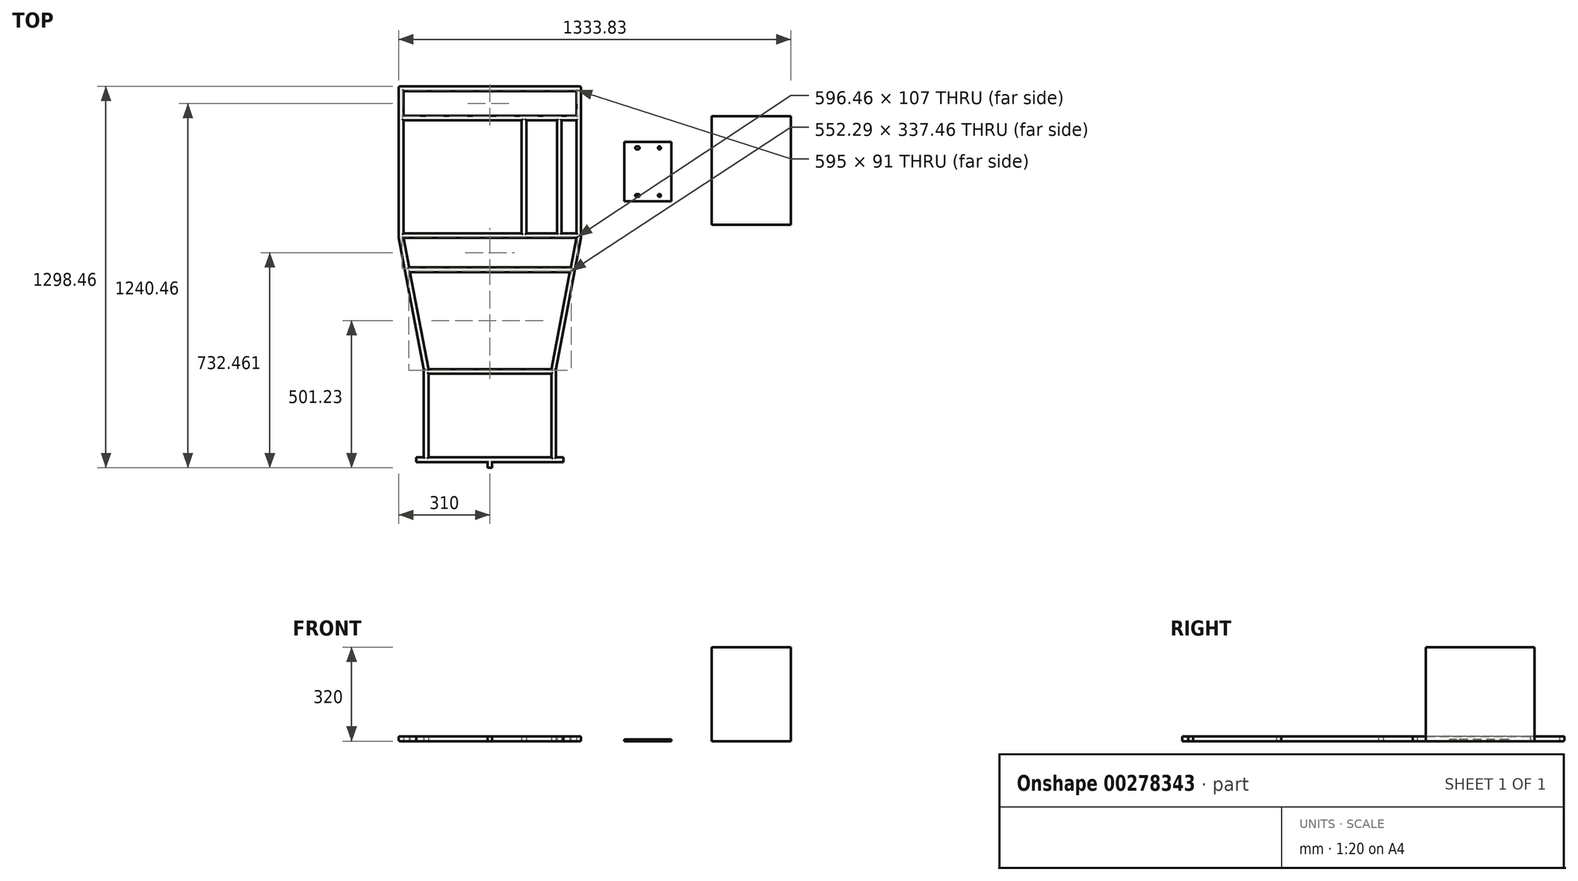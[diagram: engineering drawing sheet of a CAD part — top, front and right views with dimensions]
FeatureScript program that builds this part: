
annotation { "Feature Type Name" : "Feature", "Feature Type Description" : "" }
export const myFeature = defineFeature(function(context is Context, id is Id, definition is map)
    precondition{}
    {
        {
            var Q0;
            Q0=qCreatedBy(makeId("Top.planeOp"),FACE);
            var sketch = newSketch(context, id + "F0", { "sketchPlane" : qUnion([Q0])});
            skLineSegment(sketch, "E0", {"start": v(0, 0) * mm, "end": v(0, 589.23) * mm, "construction": true});
            skLineSegment(sketch, "E1", {"start": v(0, 0) * mm, "end": v(0, -589.23) * mm, "construction": true});
            skLineSegment(sketch, "E2", {"start": v(0, -589.23) * mm, "end": v(-225, -589.23) * mm, "construction": true});
            skLineSegment(sketch, "E3", {"start": v(0, -589.23) * mm, "end": v(225, -589.23) * mm, "construction": true});
            skLineSegment(sketch, "E4", {"start": v(0, 589.23) * mm, "end": v(-310, 589.23) * mm, "construction": true});
            skLineSegment(sketch, "E5", {"start": v(0, 589.23) * mm, "end": v(310, 589.23) * mm, "construction": true});
            skLineSegment(sketch, "E6", {"start": v(225, -589.23) * mm, "end": v(-225, -589.23) * mm});
            skLineSegment(sketch, "E7", {"start": v(310, 589.23) * mm, "end": v(-310, 589.23) * mm});
            skLineSegment(sketch, "E8.0", {"start": v(294, 573.23) * mm, "end": v(-294, 573.23) * mm});
            skLineSegment(sketch, "E8.2", {"start": v(209, -573.23) * mm, "end": v(-209, -573.23) * mm});
            skLineSegment(sketch, "E9", {"start": v(-225, -589.23) * mm, "end": v(-225, -684.23) * mm});
            skLineSegment(sketch, "E10", {"start": v(225, -589.23) * mm, "end": v(225, -684.23) * mm});
            skLineSegment(sketch, "E11", {"start": v(220, -689.23) * mm, "end": v(-220, -689.23) * mm});
            skLineSegment(sketch, "E12.0", {"start": v(209, -589.23) * mm, "end": v(209, -673.23) * mm});
            skLineSegment(sketch, "E12.1", {"start": v(209, -673.23) * mm, "end": v(-209, -673.23) * mm});
            skLineSegment(sketch, "E12.2", {"start": v(-209, -589.23) * mm, "end": v(-209, -673.23) * mm});
            skPoint(sketch, "E13.visualSharp", {"position": v(-225, -689.23) * mm});
            skArc(sketch, "E13.filletArc", {"start": v(-225, -684.23) * mm, "mid": v(-223.54, -687.77) * mm, "end": v(-220, -689.23) * mm});
            skPoint(sketch, "E14.visualSharp", {"position": v(225, -689.23) * mm});
            skArc(sketch, "E14.filletArc", {"start": v(220, -689.23) * mm, "mid": v(223.54, -687.77) * mm, "end": v(225, -684.23) * mm});
            skLineSegment(sketch, "E15", {"start": v(-310, 589.23) * mm, "end": v(-310, 684.23) * mm});
            skLineSegment(sketch, "E16", {"start": v(-305, 689.23) * mm, "end": v(305, 689.23) * mm});
            skLineSegment(sketch, "E17", {"start": v(310, 684.23) * mm, "end": v(310, 589.23) * mm});
            skLineSegment(sketch, "E18.0", {"start": v(294, 673.23) * mm, "end": v(294, 589.23) * mm});
            skLineSegment(sketch, "E18.1", {"start": v(-294, 673.23) * mm, "end": v(294, 673.23) * mm});
            skLineSegment(sketch, "E18.2", {"start": v(-294, 589.23) * mm, "end": v(-294, 673.23) * mm});
            skPoint(sketch, "E19.visualSharp", {"position": v(-310, 689.23) * mm});
            skArc(sketch, "E19.filletArc", {"start": v(-305, 689.23) * mm, "mid": v(-308.54, 687.77) * mm, "end": v(-310, 684.23) * mm});
            skPoint(sketch, "E20.visualSharp", {"position": v(310, 689.23) * mm});
            skArc(sketch, "E20.filletArc", {"start": v(310, 684.23) * mm, "mid": v(308.54, 687.77) * mm, "end": v(305, 689.23) * mm});
            skLineSegment(sketch, "E21", {"start": v(-294, 573.23) * mm, "end": v(-294, 173.23) * mm});
            skLineSegment(sketch, "E22", {"start": v(294, 573.23) * mm, "end": v(294, 173.23) * mm});
            skLineSegment(sketch, "E23", {"start": v(-310, 589.23) * mm, "end": v(-310, 173.23) * mm});
            skLineSegment(sketch, "E24", {"start": v(310, 589.23) * mm, "end": v(310, 173.23) * mm});
            skLineSegment(sketch, "E25", {"start": v(-209, -573.23) * mm, "end": v(-209, -273.23) * mm});
            skLineSegment(sketch, "E26", {"start": v(209, -573.23) * mm, "end": v(209, -273.23) * mm});
            skLineSegment(sketch, "E27", {"start": v(225, -589.23) * mm, "end": v(225, -273.23) * mm});
            skLineSegment(sketch, "E28", {"start": v(-225, -589.23) * mm, "end": v(-225, -273.23) * mm});
            skLineSegment(sketch, "E29", {"start": v(310, 173.23) * mm, "end": v(225, -273.23) * mm});
            skLineSegment(sketch, "E30", {"start": v(209, -273.23) * mm, "end": v(294, 173.23) * mm});
            skLineSegment(sketch, "E31", {"start": v(-209, -273.23) * mm, "end": v(-294, 173.23) * mm});
            skLineSegment(sketch, "E32", {"start": v(-225, -273.23) * mm, "end": v(-310, 173.23) * mm});
            skLineSegment(sketch, "E33", {"start": v(-294, 203.23) * mm, "end": v(294, 203.23) * mm, "construction": true});
            skLineSegment(sketch, "E34", {"start": v(-209, -273.23) * mm, "end": v(209, -273.23) * mm});
            skLineSegment(sketch, "E35", {"start": v(-209, -289.23) * mm, "end": v(209, -289.23) * mm});
            skLineSegment(sketch, "E36", {"start": v(294, 173.23) * mm, "end": v(-294, 173.23) * mm});
            skLineSegment(sketch, "E37", {"start": v(-294, 189.23) * mm, "end": v(294, 189.23) * mm});
            skLineSegment(sketch, "E38", {"start": v(244, 573.23) * mm, "end": v(244, 189.23) * mm});
            skLineSegment(sketch, "E39", {"start": v(228, 573.23) * mm, "end": v(228, 189.23) * mm});
            skLineSegment(sketch, "E40", {"start": v(124, 573.23) * mm, "end": v(124, 189.23) * mm});
            skLineSegment(sketch, "E41", {"start": v(108, 573.23) * mm, "end": v(108, 189.23) * mm});
            skLineSegment(sketch, "E42", {"start": v(116, 573.23) * mm, "end": v(116, 189.23) * mm, "construction": true});
            skLineSegment(sketch, "E43", {"start": v(236, 189.23) * mm, "end": v(236, 573.23) * mm, "construction": true});
            skLineSegment(sketch, "E44", {"start": v(-271.92, 57.23) * mm, "end": v(271.92, 57.23) * mm});
            skLineSegment(sketch, "E45", {"start": v(271.92, 57.23) * mm, "end": v(274.96, 73.23) * mm});
            skLineSegment(sketch, "E46", {"start": v(274.96, 73.23) * mm, "end": v(-274.96, 73.23) * mm});
            skLineSegment(sketch, "E47", {"start": v(225, -589.23) * mm, "end": v(250, -589.23) * mm});
            skLineSegment(sketch, "E48", {"start": v(250, -589.23) * mm, "end": v(250, -573.23) * mm});
            skLineSegment(sketch, "E49", {"start": v(250, -573.23) * mm, "end": v(225, -573.23) * mm});
            skLineSegment(sketch, "E50", {"start": v(-225, -589.23) * mm, "end": v(-250, -589.23) * mm});
            skLineSegment(sketch, "E51", {"start": v(-250, -589.23) * mm, "end": v(-250, -573.23) * mm});
            skLineSegment(sketch, "E52", {"start": v(-250, -573.23) * mm, "end": v(-225, -573.23) * mm});
            skLineSegment(sketch, "E53", {"start": v(-8, -589.23) * mm, "end": v(-8, -609.23) * mm});
            skLineSegment(sketch, "E54", {"start": v(-8, -609.23) * mm, "end": v(8, -609.23) * mm});
            skLineSegment(sketch, "E55", {"start": v(8, -609.23) * mm, "end": v(8, -589.23) * mm});
            skLineSegment(sketch, "E56", {"start": v(0, -589.23) * mm, "end": v(0, -609.23) * mm, "construction": true});
            skSolve(sketch);
        }
        {
            var Q0;
            {var subQ0=sQuery(id+"F0.wireOp",EDGE,"E15");Q0=makeQuery(id+"F0.imprint","IMPRINT",FACE,{"disambiguationData":[TD([[makeQuery(id+"F0.imprint","IMPRINT",EDGE,{"derivedFrom":subQ0}),-1.0]])]});}
            var Q1;
            {var subQ8=sQuery(id+"F0.wireOp",EDGE,"E8.0");Q1=makeQuery(id+"F0.imprint","IMPRINT",FACE,{"disambiguationData":[TD([[makeQuery(id+"F0.imprint","IMPRINT",EDGE,{"derivedFrom":subQ8}),-1.0]])]});}
            var Q2;
            {var subQ0=sQuery(id+"F0.wireOp",EDGE,"E33");Q2=makeQuery(id+"F0.imprint","IMPRINT",FACE,{"disambiguationData":[TD([[makeQuery(id+"F0.imprint","IMPRINT",EDGE,{"derivedFrom":subQ0}),1.0]])]});}
            var Q3;
            {var subQ0=sQuery(id+"F0.wireOp",EDGE,"E34");Q3=makeQuery(id+"F0.imprint","IMPRINT",FACE,{"disambiguationData":[TD([[makeQuery(id+"F0.imprint","IMPRINT",EDGE,{"derivedFrom":subQ0}),-1.0]])]});}
            var Q4;
            {var subQ0=sQuery(id+"F0.wireOp",EDGE,"E36");Q4=makeQuery(id+"F0.imprint","IMPRINT",FACE,{"disambiguationData":[TD([[makeQuery(id+"F0.imprint","IMPRINT",EDGE,{"derivedFrom":subQ0}),-1.0]])]});}
            var Q5;
            {var subQ0=sQuery(id+"F0.wireOp",EDGE,"E40");Q5=makeQuery(id+"F0.imprint","IMPRINT",FACE,{"disambiguationData":[TD([[makeQuery(id+"F0.imprint","IMPRINT",EDGE,{"derivedFrom":subQ0}),-1.0]])]});}
            var Q6;
            {var subQ0=sQuery(id+"F0.wireOp",EDGE,"E38");Q6=makeQuery(id+"F0.imprint","IMPRINT",FACE,{"disambiguationData":[TD([[makeQuery(id+"F0.imprint","IMPRINT",EDGE,{"derivedFrom":subQ0}),-1.0]])]});}
            var Q7;
            {var subQ0=sQuery(id+"F0.wireOp",EDGE,"E44");Q7=makeQuery(id+"F0.imprint","IMPRINT",FACE,{"disambiguationData":[TD([[makeQuery(id+"F0.imprint","IMPRINT",EDGE,{"derivedFrom":subQ0}),1.0]])]});}
            var Q8;
            {var subQ0=sQuery(id+"F0.wireOp",EDGE,"E50");Q8=makeQuery(id+"F0.imprint","IMPRINT",FACE,{"disambiguationData":[TD([[makeQuery(id+"F0.imprint","IMPRINT",EDGE,{"derivedFrom":subQ0}),-1.0]])]});}
            var Q9;
            {var subQ0=sQuery(id+"F0.wireOp",EDGE,"E47");Q9=makeQuery(id+"F0.imprint","IMPRINT",FACE,{"disambiguationData":[TD([[makeQuery(id+"F0.imprint","IMPRINT",EDGE,{"derivedFrom":subQ0}),1.0]])]});}
            var Q10;
            {var subQ0=sQuery(id+"F0.wireOp",EDGE,"E53");Q10=makeQuery(id+"F0.imprint","IMPRINT",FACE,{"disambiguationData":[TD([[makeQuery(id+"F0.imprint","IMPRINT",EDGE,{"derivedFrom":subQ0}),1.0]])]});}
            extrude(context, id + "F1", {"entities" : qUnion([Q0, Q1, Q2, Q3, Q4, Q5, Q6, Q7, Q8, Q9, Q10]), "depth" : 16 * mm});
        }
        {
            var Q0;
            Q0=makeQuery(id+"F1.opExtrude","CAP_EDGE",EDGE,{"disambiguationData":[OSD([sQuery(id+"F0.wireOp",EDGE,"E10")])],"isStart":false});
            var Q1;
            Q1=makeQuery(id+"F1.opExtrude","CAP_EDGE",EDGE,{"disambiguationData":[OSD([sQuery(id+"F0.wireOp",EDGE,"xuW9dsa4-weEu-yKkH-qgbv-HWIhfIHViFJe")])],"isStart":false});
            var Q2;
            Q2=makeQuery(id+"F1.opExtrude","CAP_EDGE",EDGE,{"disambiguationData":[OSD([sQuery(id+"F0.wireOp",EDGE,"E6")])],"isStart":false});
            var Q3;
            Q3=makeQuery(id+"F1.opExtrude","CAP_EDGE",EDGE,{"disambiguationData":[OSD([sQuery(id+"F0.wireOp",EDGE,"E8.2")])],"isStart":false});
            var Q4;
            Q4=makeQuery(id+"F1.opExtrude","CAP_EDGE",EDGE,{"disambiguationData":[OSD([sQuery(id+"F0.wireOp",EDGE,"E8.3")])],"isStart":false});
            var Q5;
            Q5=makeQuery(id+"F1.opExtrude","CAP_EDGE",EDGE,{"disambiguationData":[OSD([sQuery(id+"F0.wireOp",EDGE,"E12.2")])],"isStart":false});
            var Q6;
            Q6=makeQuery(id+"F1.opExtrude","CAP_EDGE",EDGE,{"disambiguationData":[OSD([sQuery(id+"F0.wireOp",EDGE,"E8.0")])],"isStart":false});
            var Q7;
            Q7=makeQuery(id+"F1.opExtrude","CAP_EDGE",EDGE,{"disambiguationData":[OSD([sQuery(id+"F0.wireOp",EDGE,"E7")])],"isStart":false});
            var Q8;
            Q8=makeQuery(id+"F1.opExtrude","CAP_EDGE",EDGE,{"disambiguationData":[OSD([sQuery(id+"F0.wireOp",EDGE,"E18.1")])],"isStart":false});
            var Q9;
            Q9=makeQuery(id+"F1.opExtrude","CAP_EDGE",EDGE,{"disambiguationData":[OSD([sQuery(id+"F0.wireOp",EDGE,"E16")])],"isStart":false});
            var Q10;
            Q10=makeQuery(id+"F1.opExtrude","CAP_EDGE",EDGE,{"disambiguationData":[OSD([sQuery(id+"F0.wireOp",EDGE,"E17")])],"isStart":false});
            var Q11;
            Q11=makeQuery(id+"F1.opExtrude","CAP_EDGE",EDGE,{"disambiguationData":[OSD([sQuery(id+"F0.wireOp",EDGE,"E18.0")])],"isStart":false});
            var Q12;
            Q12=makeQuery(id+"F1.opExtrude","CAP_EDGE",EDGE,{"disambiguationData":[OSD([sQuery(id+"F0.wireOp",EDGE,"E18.2")])],"isStart":false});
            var Q13;
            Q13=makeQuery(id+"F1.opExtrude","CAP_EDGE",EDGE,{"disambiguationData":[OSD([sQuery(id+"F0.wireOp",EDGE,"kNVx2aqo-1R29-r8ME-eJTo-0D4SkdkJlZAj")])],"isStart":false});
            var Q14;
            Q14=makeQuery(id+"F1.opExtrude","CAP_EDGE",EDGE,{"disambiguationData":[OSD([sQuery(id+"F0.wireOp",EDGE,"kNVx2aqo-1R29-r8ME-eJTo-0D4SkdkJlZAj")])],"isStart":true});
            var Q15;
            Q15=makeQuery(id+"F1.opExtrude","CAP_EDGE",EDGE,{"disambiguationData":[OSD([sQuery(id+"F0.wireOp",EDGE,"E15")])],"isStart":false});
            var Q16;
            Q16=makeQuery(id+"F1.opExtrude","CAP_EDGE",EDGE,{"disambiguationData":[OSD([sQuery(id+"F0.wireOp",EDGE,"E16")])],"isStart":true});
            var Q17;
            Q17=makeQuery(id+"F1.opExtrude","CAP_EDGE",EDGE,{"disambiguationData":[OSD([sQuery(id+"F0.wireOp",EDGE,"E8.1")])],"isStart":true});
            var Q18;
            Q18=makeQuery(id+"F1.opExtrude","CAP_EDGE",EDGE,{"disambiguationData":[OSD([sQuery(id+"F0.wireOp",EDGE,"E8.2")])],"isStart":true});
            var Q19;
            Q19=makeQuery(id+"F1.opExtrude","CAP_EDGE",EDGE,{"disambiguationData":[OSD([sQuery(id+"F0.wireOp",EDGE,"E12.1")])],"isStart":true});
            var Q20;
            Q20=makeQuery(id+"F1.opExtrude","CAP_EDGE",EDGE,{"disambiguationData":[OSD([sQuery(id+"F0.wireOp",EDGE,"E12.2")])],"isStart":true});
            var Q21;
            Q21=makeQuery(id+"F1.opExtrude","CAP_EDGE",EDGE,{"disambiguationData":[OSD([sQuery(id+"F0.wireOp",EDGE,"E12.0")])],"isStart":true});
            var Q22;
            Q22=makeQuery(id+"F1.opExtrude","CAP_EDGE",EDGE,{"disambiguationData":[OSD([sQuery(id+"F0.wireOp",EDGE,"E11")])],"isStart":true});
            var Q23;
            Q23=makeQuery(id+"F1.opExtrude","CAP_EDGE",EDGE,{"disambiguationData":[OSD([sQuery(id+"F0.wireOp",EDGE,"xuW9dsa4-weEu-yKkH-qgbv-HWIhfIHViFJe")])],"isStart":true});
            var Q24;
            Q24=makeQuery(id+"F1.opExtrude","CAP_EDGE",EDGE,{"disambiguationData":[OSD([sQuery(id+"F0.wireOp",EDGE,"E18.1")])],"isStart":true});
            var Q25;
            Q25=makeQuery(id+"F1.opExtrude","CAP_EDGE",EDGE,{"disambiguationData":[OSD([sQuery(id+"F0.wireOp",EDGE,"E8.3")])],"isStart":true});
            var Q26;
            Q26=makeQuery(id+"F1.opExtrude","CAP_EDGE",EDGE,{"disambiguationData":[OSD([sQuery(id+"F0.wireOp",EDGE,"E12.0")])],"isStart":false});
            var Q27;
            Q27=makeQuery(id+"F1.opExtrude","CAP_EDGE",EDGE,{"disambiguationData":[OSD([sQuery(id+"F0.wireOp",EDGE,"E12.1")])],"isStart":false});
            var Q28;
            Q28=makeQuery(id+"F1.opExtrude","CAP_EDGE",EDGE,{"disambiguationData":[OSD([sQuery(id+"F0.wireOp",EDGE,"E8.1")])],"isStart":false});
            var Q29;
            Q29=makeQuery(id+"F1.opExtrude","CAP_EDGE",EDGE,{"disambiguationData":[OSD([sQuery(id+"F0.wireOp",EDGE,"LtXW5kV8-ZuAr-H9Sn-P5R5-MpdMKfMSttiU")])],"isStart":false});
            var Q30;
            Q30=makeQuery(id+"F1.opExtrude","CAP_EDGE",EDGE,{"disambiguationData":[OSD([sQuery(id+"F0.wireOp",EDGE,"e5hs6JYA-LP03-OFxl-pStV-6oDWOiMYZsi8")])],"isStart":false});
            var Q31;
            Q31=makeQuery(id+"F1.opExtrude","CAP_EDGE",EDGE,{"disambiguationData":[OSD([sQuery(id+"F0.wireOp",EDGE,"e5hs6JYA-LP03-OFxl-pStV-6oDWOiMYZsi8")])],"isStart":true});
            var Q32;
            Q32=makeQuery(id+"F1.opExtrude","CAP_EDGE",EDGE,{"disambiguationData":[OSD([sQuery(id+"F0.wireOp",EDGE,"LtXW5kV8-ZuAr-H9Sn-P5R5-MpdMKfMSttiU")])],"isStart":true});
            var Q33;
            {var subQ0=sQuery(id+"F0.wireOp",EDGE,"E21");Q33=makeQuery(id+"F1.opExtrude","CAP_EDGE",EDGE,{"disambiguationData":[OSD([subQ0]),TDD([makeQuery(id+"F0.imprint","IMPRINT",EDGE,{"disambiguationData":[TD([[makeQuery(id+"F0.imprint","INTERSECT",VERTEX,{"derivedFrom":[sQuery(id+"F0.wireOp",EDGE,"E8.0"),subQ0]}),-1.0]])],"derivedFrom":subQ0})])],"isStart":false});}
            var Q34;
            {var subQ0=sQuery(id+"F0.wireOp",EDGE,"E22");Q34=makeQuery(id+"F1.opExtrude","CAP_EDGE",EDGE,{"disambiguationData":[OSD([subQ0]),TDD([makeQuery(id+"F0.imprint","IMPRINT",EDGE,{"disambiguationData":[TD([[makeQuery(id+"F0.imprint","INTERSECT",VERTEX,{"derivedFrom":[sQuery(id+"F0.wireOp",EDGE,"E8.0"),subQ0]}),-1.0]])],"derivedFrom":subQ0})])],"isStart":false});}
            var Q35;
            Q35=makeQuery(id+"F1.opExtrude","CAP_EDGE",EDGE,{"disambiguationData":[OSD([sQuery(id+"F0.wireOp",EDGE,"DEUJzCMv-8Ogu-k544-0Mz8-tlRbfYKvvYv5")])],"isStart":false});
            var Q36;
            Q36=makeQuery(id+"F1.opExtrude","CAP_EDGE",EDGE,{"disambiguationData":[OSD([sQuery(id+"F0.wireOp",EDGE,"E33")])],"isStart":false});
            var Q37;
            {var subQ0=sQuery(id+"F0.wireOp",EDGE,"E21");Q37=makeQuery(id+"F1.opExtrude","CAP_EDGE",EDGE,{"disambiguationData":[OSD([subQ0]),TDD([makeQuery(id+"F0.imprint","IMPRINT",EDGE,{"disambiguationData":[TD([[makeQuery(id+"F0.imprint","INTERSECT",VERTEX,{"derivedFrom":[subQ0,sQuery(id+"F0.wireOp",EDGE,"E31")]}),1.0]])],"derivedFrom":subQ0})])],"isStart":false});}
            var Q38;
            {var subQ0=sQuery(id+"F0.wireOp",EDGE,"E22");Q38=makeQuery(id+"F1.opExtrude","CAP_EDGE",EDGE,{"disambiguationData":[OSD([subQ0]),TDD([makeQuery(id+"F0.imprint","IMPRINT",EDGE,{"disambiguationData":[TD([[makeQuery(id+"F0.imprint","INTERSECT",VERTEX,{"derivedFrom":[subQ0,sQuery(id+"F0.wireOp",EDGE,"E30")]}),1.0]])],"derivedFrom":subQ0})])],"isStart":false});}
            var Q39;
            Q39=makeQuery(id+"F1.opExtrude","CAP_EDGE",EDGE,{"disambiguationData":[OSD([sQuery(id+"F0.wireOp",EDGE,"E31")])],"isStart":false});
            var Q40;
            Q40=makeQuery(id+"F1.opExtrude","CAP_EDGE",EDGE,{"disambiguationData":[OSD([sQuery(id+"F0.wireOp",EDGE,"E30")])],"isStart":false});
            var Q41;
            Q41=makeQuery(id+"F1.opExtrude","CAP_EDGE",EDGE,{"disambiguationData":[OSD([sQuery(id+"F0.wireOp",EDGE,"E34")])],"isStart":false});
            var Q42;
            Q42=makeQuery(id+"F1.opExtrude","CAP_EDGE",EDGE,{"disambiguationData":[OSD([sQuery(id+"F0.wireOp",EDGE,"E35")])],"isStart":false});
            var Q43;
            Q43=makeQuery(id+"F1.opExtrude","CAP_EDGE",EDGE,{"disambiguationData":[OSD([sQuery(id+"F0.wireOp",EDGE,"E32")])],"isStart":false});
            var Q44;
            Q44=makeQuery(id+"F1.opExtrude","CAP_EDGE",EDGE,{"disambiguationData":[OSD([sQuery(id+"F0.wireOp",EDGE,"E25")])],"isStart":false});
            var Q45;
            Q45=makeQuery(id+"F1.opExtrude","CAP_EDGE",EDGE,{"disambiguationData":[OSD([sQuery(id+"F0.wireOp",EDGE,"E26")])],"isStart":false});
            var Q46;
            Q46=makeQuery(id+"F1.opExtrude","CAP_EDGE",EDGE,{"disambiguationData":[OSD([sQuery(id+"F0.wireOp",EDGE,"E29")])],"isStart":false});
            var Q47;
            Q47=makeQuery(id+"F1.opExtrude","CAP_EDGE",EDGE,{"disambiguationData":[OSD([sQuery(id+"F0.wireOp",EDGE,"E35")])],"isStart":true});
            var Q48;
            Q48=makeQuery(id+"F1.opExtrude","CAP_EDGE",EDGE,{"disambiguationData":[OSD([sQuery(id+"F0.wireOp",EDGE,"E34")])],"isStart":true});
            var Q49;
            Q49=makeQuery(id+"F1.opExtrude","CAP_EDGE",EDGE,{"disambiguationData":[OSD([sQuery(id+"F0.wireOp",EDGE,"E30")])],"isStart":true});
            var Q50;
            Q50=makeQuery(id+"F1.opExtrude","CAP_EDGE",EDGE,{"disambiguationData":[OSD([sQuery(id+"F0.wireOp",EDGE,"E29")])],"isStart":true});
            var Q51;
            Q51=makeQuery(id+"F1.opExtrude","CAP_EDGE",EDGE,{"disambiguationData":[OSD([sQuery(id+"F0.wireOp",EDGE,"E31")])],"isStart":true});
            var Q52;
            Q52=makeQuery(id+"F1.opExtrude","CAP_EDGE",EDGE,{"disambiguationData":[OSD([sQuery(id+"F0.wireOp",EDGE,"E9"),sQuery(id+"F0.wireOp",EDGE,"E28")])],"isStart":true});
            var Q53;
            Q53=makeQuery(id+"F1.opExtrude","CAP_EDGE",EDGE,{"disambiguationData":[OSD([sQuery(id+"F0.wireOp",EDGE,"E32")])],"isStart":true});
            var Q54;
            Q54=makeQuery(id+"F1.opExtrude","CAP_EDGE",EDGE,{"disambiguationData":[OSD([sQuery(id+"F0.wireOp",EDGE,"E33")])],"isStart":true});
            var Q55;
            Q55=makeQuery(id+"F1.opExtrude","CAP_EDGE",EDGE,{"disambiguationData":[OSD([sQuery(id+"F0.wireOp",EDGE,"DEUJzCMv-8Ogu-k544-0Mz8-tlRbfYKvvYv5")])],"isStart":true});
            var Q56;
            {var subQ0=sQuery(id+"F0.wireOp",EDGE,"E22");Q56=makeQuery(id+"F1.opExtrude","CAP_EDGE",EDGE,{"disambiguationData":[OSD([subQ0]),TDD([makeQuery(id+"F0.imprint","IMPRINT",EDGE,{"disambiguationData":[TD([[makeQuery(id+"F0.imprint","INTERSECT",VERTEX,{"derivedFrom":[sQuery(id+"F0.wireOp",EDGE,"E8.0"),subQ0]}),-1.0]])],"derivedFrom":subQ0})])],"isStart":true});}
            var Q57;
            {var subQ0=sQuery(id+"F0.wireOp",EDGE,"E22");Q57=makeQuery(id+"F1.opExtrude","CAP_EDGE",EDGE,{"disambiguationData":[OSD([subQ0]),TDD([makeQuery(id+"F0.imprint","IMPRINT",EDGE,{"disambiguationData":[TD([[makeQuery(id+"F0.imprint","INTERSECT",VERTEX,{"derivedFrom":[subQ0,sQuery(id+"F0.wireOp",EDGE,"E30")]}),1.0]])],"derivedFrom":subQ0})])],"isStart":true});}
            var Q58;
            {var subQ0=sQuery(id+"F0.wireOp",EDGE,"E21");Q58=makeQuery(id+"F1.opExtrude","CAP_EDGE",EDGE,{"disambiguationData":[OSD([subQ0]),TDD([makeQuery(id+"F0.imprint","IMPRINT",EDGE,{"disambiguationData":[TD([[makeQuery(id+"F0.imprint","INTERSECT",VERTEX,{"derivedFrom":[subQ0,sQuery(id+"F0.wireOp",EDGE,"E31")]}),1.0]])],"derivedFrom":subQ0})])],"isStart":true});}
            var Q59;
            Q59=makeQuery(id+"F1.opExtrude","CAP_EDGE",EDGE,{"disambiguationData":[OSD([sQuery(id+"F0.wireOp",EDGE,"E8.0")])],"isStart":true});
            var Q60;
            Q60=makeQuery(id+"F1.opExtrude","CAP_EDGE",EDGE,{"disambiguationData":[OSD([sQuery(id+"F0.wireOp",EDGE,"E7")])],"isStart":true});
            var Q61;
            Q61=makeQuery(id+"F1.opExtrude","CAP_EDGE",EDGE,{"disambiguationData":[OSD([sQuery(id+"F0.wireOp",EDGE,"E18.0")])],"isStart":true});
            var Q62;
            Q62=makeQuery(id+"F1.opExtrude","CAP_EDGE",EDGE,{"disambiguationData":[OSD([sQuery(id+"F0.wireOp",EDGE,"E17"),sQuery(id+"F0.wireOp",EDGE,"E24")])],"isStart":true});
            var Q63;
            {var subQ0=sQuery(id+"F0.wireOp",EDGE,"E21");Q63=makeQuery(id+"F1.opExtrude","CAP_EDGE",EDGE,{"disambiguationData":[OSD([subQ0]),TDD([makeQuery(id+"F0.imprint","IMPRINT",EDGE,{"disambiguationData":[TD([[makeQuery(id+"F0.imprint","INTERSECT",VERTEX,{"derivedFrom":[sQuery(id+"F0.wireOp",EDGE,"E8.0"),subQ0]}),-1.0]])],"derivedFrom":subQ0})])],"isStart":true});}
            var Q64;
            Q64=makeQuery(id+"F1.opExtrude","CAP_EDGE",EDGE,{"disambiguationData":[OSD([sQuery(id+"F0.wireOp",EDGE,"E18.2")])],"isStart":true});
            var Q65;
            Q65=makeQuery(id+"F1.opExtrude","CAP_EDGE",EDGE,{"disambiguationData":[OSD([sQuery(id+"F0.wireOp",EDGE,"E26")])],"isStart":true});
            var Q66;
            Q66=makeQuery(id+"F1.opExtrude","CAP_EDGE",EDGE,{"disambiguationData":[OSD([sQuery(id+"F0.wireOp",EDGE,"E36")])],"isStart":false});
            var Q67;
            Q67=makeQuery(id+"F1.opExtrude","CAP_EDGE",EDGE,{"disambiguationData":[OSD([sQuery(id+"F0.wireOp",EDGE,"E37")])],"isStart":false});
            var Q68;
            Q68=makeQuery(id+"F1.opExtrude","CAP_EDGE",EDGE,{"disambiguationData":[OSD([sQuery(id+"F0.wireOp",EDGE,"E41")])],"isStart":false});
            var Q69;
            Q69=makeQuery(id+"F1.opExtrude","CAP_EDGE",EDGE,{"disambiguationData":[OSD([sQuery(id+"F0.wireOp",EDGE,"E40")])],"isStart":false});
            var Q70;
            Q70=makeQuery(id+"F1.opExtrude","CAP_EDGE",EDGE,{"disambiguationData":[OSD([sQuery(id+"F0.wireOp",EDGE,"E39")])],"isStart":false});
            var Q71;
            Q71=makeQuery(id+"F1.opExtrude","CAP_EDGE",EDGE,{"disambiguationData":[OSD([sQuery(id+"F0.wireOp",EDGE,"E38")])],"isStart":false});
            var Q72;
            Q72=makeQuery(id+"F1.opExtrude","CAP_EDGE",EDGE,{"disambiguationData":[OSD([sQuery(id+"F0.wireOp",EDGE,"E41")])],"isStart":true});
            var Q73;
            Q73=makeQuery(id+"F1.opExtrude","CAP_EDGE",EDGE,{"disambiguationData":[OSD([sQuery(id+"F0.wireOp",EDGE,"E39")])],"isStart":true});
            var Q74;
            Q74=makeQuery(id+"F1.opExtrude","CAP_EDGE",EDGE,{"disambiguationData":[OSD([sQuery(id+"F0.wireOp",EDGE,"E38")])],"isStart":true});
            var Q75;
            Q75=makeQuery(id+"F1.opExtrude","CAP_EDGE",EDGE,{"disambiguationData":[OSD([sQuery(id+"F0.wireOp",EDGE,"E40")])],"isStart":true});
            var Q76;
            Q76=makeQuery(id+"F1.opExtrude","CAP_EDGE",EDGE,{"disambiguationData":[OSD([sQuery(id+"F0.wireOp",EDGE,"E46")])],"isStart":false});
            var Q77;
            Q77=makeQuery(id+"F1.opExtrude","CAP_EDGE",EDGE,{"disambiguationData":[OSD([sQuery(id+"F0.wireOp",EDGE,"E44")])],"isStart":false});
            var Q78;
            Q78=makeQuery(id+"F1.opExtrude","CAP_EDGE",EDGE,{"disambiguationData":[OSD([sQuery(id+"F0.wireOp",EDGE,"E46")])],"isStart":true});
            var Q79;
            Q79=makeQuery(id+"F1.opExtrude","CAP_EDGE",EDGE,{"disambiguationData":[OSD([sQuery(id+"F0.wireOp",EDGE,"E44")])],"isStart":true});
            var Q80;
            Q80=makeQuery(id+"F1.opExtrude","CAP_EDGE",EDGE,{"disambiguationData":[OSD([sQuery(id+"F0.wireOp",EDGE,"E36")])],"isStart":true});
            var Q81;
            {var subQ0=sQuery(id+"F0.wireOp",EDGE,"E37");Q81=makeQuery(id+"F1.opExtrude","CAP_EDGE",EDGE,{"disambiguationData":[OSD([subQ0]),TDD([makeQuery(id+"F0.imprint","IMPRINT",EDGE,{"disambiguationData":[TD([[makeQuery(id+"F0.imprint","INTERSECT",VERTEX,{"derivedFrom":[sQuery(id+"F0.wireOp",EDGE,"E21"),subQ0]}),-1.0]])],"derivedFrom":subQ0})])],"isStart":true});}
            var Q82;
            Q82=makeQuery(id+"F1.opExtrude","CAP_EDGE",EDGE,{"disambiguationData":[OSD([sQuery(id+"F0.wireOp",EDGE,"E6")])],"isStart":true});
            var Q83;
            Q83=makeQuery(id+"F1.opExtrude","CAP_EDGE",EDGE,{"disambiguationData":[OSD([sQuery(id+"F0.wireOp",EDGE,"E52")])],"isStart":false});
            var Q84;
            Q84=makeQuery(id+"F1.opExtrude","CAP_EDGE",EDGE,{"disambiguationData":[OSD([sQuery(id+"F0.wireOp",EDGE,"E50")])],"isStart":true});
            var Q85;
            Q85=makeQuery(id+"F1.opExtrude","CAP_EDGE",EDGE,{"disambiguationData":[OSD([sQuery(id+"F0.wireOp",EDGE,"E52")])],"isStart":true});
            var Q86;
            Q86=makeQuery(id+"F1.opExtrude","CAP_EDGE",EDGE,{"disambiguationData":[OSD([sQuery(id+"F0.wireOp",EDGE,"E50")])],"isStart":false});
            var Q87;
            Q87=makeQuery(id+"F1.opExtrude","CAP_EDGE",EDGE,{"disambiguationData":[OSD([sQuery(id+"F0.wireOp",EDGE,"E49")])],"isStart":false});
            var Q88;
            Q88=makeQuery(id+"F1.opExtrude","CAP_EDGE",EDGE,{"disambiguationData":[OSD([sQuery(id+"F0.wireOp",EDGE,"E47")])],"isStart":false});
            var Q89;
            Q89=makeQuery(id+"F1.opExtrude","CAP_EDGE",EDGE,{"disambiguationData":[OSD([sQuery(id+"F0.wireOp",EDGE,"E47")])],"isStart":true});
            var Q90;
            Q90=makeQuery(id+"F1.opExtrude","CAP_EDGE",EDGE,{"disambiguationData":[OSD([sQuery(id+"F0.wireOp",EDGE,"E49")])],"isStart":true});
            var Q91;
            Q91=makeQuery(id+"F1.opExtrude","CAP_EDGE",EDGE,{"disambiguationData":[OSD([sQuery(id+"F0.wireOp",EDGE,"E27")])],"isStart":true});
            var Q92;
            Q92=makeQuery(id+"F1.opExtrude","CAP_EDGE",EDGE,{"disambiguationData":[OSD([sQuery(id+"F0.wireOp",EDGE,"E27")])],"isStart":false});
            var Q93;
            Q93=makeQuery(id+"F1.opExtrude","CAP_EDGE",EDGE,{"disambiguationData":[OSD([sQuery(id+"F0.wireOp",EDGE,"E28")])],"isStart":false});
            var Q94;
            Q94=makeQuery(id+"F1.opExtrude","CAP_EDGE",EDGE,{"disambiguationData":[OSD([sQuery(id+"F0.wireOp",EDGE,"E25")])],"isStart":true});
            fillet(context, id + "F2", {"entities" : qUnion([Q0, Q1, Q2, Q3, Q4, Q5, Q6, Q7, Q8, Q9, Q10, Q11, Q12, Q13, Q14, Q15, Q16, Q17, Q18, Q19, Q20, Q21, Q22, Q23, Q24, Q25, Q26, Q27, Q28, Q29, Q30, Q31, Q32, Q33, Q34, Q35, Q36, Q37, Q38, Q39, Q40, Q41, Q42, Q43, Q44, Q45, Q46, Q47, Q48, Q49, Q50, Q51, Q52, Q53, Q54, Q55, Q56, Q57, Q58, Q59, Q60, Q61, Q62, Q63, Q64, Q65, Q66, Q67, Q68, Q69, Q70, Q71, Q72, Q73, Q74, Q75, Q76, Q77, Q78, Q79, Q80, Q81, Q82, Q83, Q84, Q85, Q86, Q87, Q88, Q89, Q90, Q91, Q92, Q93, Q94]), "radius" : 3.5 * mm, "tangentPropagation" : true, "allowEdgeOverflow" : false});
        }
        {
            var Q0;
            Q0=qCreatedBy(makeId("Top.planeOp"),FACE);
            var sketch = newSketch(context, id + "F3", { "sketchPlane" : qUnion([Q0])});
            skLineSegment(sketch, "E57.bottom", {"start": v(753.83, 218.05) * mm, "end": v(1023.83, 218.05) * mm});
            skLineSegment(sketch, "E57.top", {"start": v(753.83, 588.05) * mm, "end": v(1023.83, 588.05) * mm});
            skLineSegment(sketch, "E57.left", {"start": v(753.83, 218.05) * mm, "end": v(753.83, 588.05) * mm});
            skLineSegment(sketch, "E57.right", {"start": v(1023.83, 218.05) * mm, "end": v(1023.83, 588.05) * mm});
            skSolve(sketch);
        }
        {
            var Q0;
            Q0=makeQuery(id+"F3.imprint","IMPRINT",FACE,{"disambiguationData":[TD([[makeQuery(id+"F3.imprint","IMPRINT",EDGE,{"derivedFrom":sQuery(id+"F3.wireOp",EDGE,"E57.bottom")}),1.0]])]});
            extrude(context, id + "F4", {"entities" : qUnion([Q0]), "depth" : 320 * mm});
        }
        {
            var Q0;
            Q0=qCreatedBy(makeId("Top.planeOp"),FACE);
            var sketch = newSketch(context, id + "F5", { "sketchPlane" : qUnion([Q0])});
            skLineSegment(sketch, "E58.bottom", {"start": v(499.1, 322.6) * mm, "end": v(504.1, 322.6) * mm});
            skLineSegment(sketch, "E58.top", {"start": v(499.1, 312.6) * mm, "end": v(504.1, 312.6) * mm});
            skLineSegment(sketch, "E58.left", {"start": v(494.1, 317.6) * mm, "end": v(494.1, 317.6) * mm});
            skLineSegment(sketch, "E58.right", {"start": v(509.1, 317.6) * mm, "end": v(509.1, 317.6) * mm});
            skPoint(sketch, "E59.oppositeSnap0", {"position": v(509.1, 317.6) * mm});
            skLineSegment(sketch, "E59.bottom", {"start": v(499.1, 484.6) * mm, "end": v(504.1, 484.6) * mm});
            skLineSegment(sketch, "E59.top", {"start": v(499.1, 474.6) * mm, "end": v(504.1, 474.6) * mm});
            skLineSegment(sketch, "E59.left", {"start": v(494.1, 479.6) * mm, "end": v(494.1, 479.6) * mm});
            skLineSegment(sketch, "E59.right", {"start": v(509.1, 479.6) * mm, "end": v(509.1, 479.6) * mm});
            skPoint(sketch, "E60.visualSharp", {"position": v(494.1, 474.6) * mm});
            skArc(sketch, "E60.filletArc", {"start": v(494.1, 479.6) * mm, "mid": v(495.56, 476.07) * mm, "end": v(499.1, 474.6) * mm});
            skPoint(sketch, "E61.visualSharp", {"position": v(494.1, 484.6) * mm});
            skArc(sketch, "E61.filletArc", {"start": v(499.1, 484.6) * mm, "mid": v(495.56, 483.14) * mm, "end": v(494.1, 479.6) * mm});
            skPoint(sketch, "E62.visualSharp", {"position": v(509.1, 484.6) * mm});
            skArc(sketch, "E62.filletArc", {"start": v(509.1, 479.6) * mm, "mid": v(507.63, 483.14) * mm, "end": v(504.1, 484.6) * mm});
            skPoint(sketch, "E63.visualSharp", {"position": v(509.1, 474.6) * mm});
            skArc(sketch, "E63.filletArc", {"start": v(504.1, 474.6) * mm, "mid": v(507.63, 476.07) * mm, "end": v(509.1, 479.6) * mm});
            skPoint(sketch, "E64.visualSharp", {"position": v(509.1, 322.6) * mm});
            skArc(sketch, "E64.filletArc", {"start": v(509.1, 317.6) * mm, "mid": v(507.63, 321.14) * mm, "end": v(504.1, 322.6) * mm});
            skPoint(sketch, "E65.visualSharp", {"position": v(494.1, 322.6) * mm});
            skArc(sketch, "E65.filletArc", {"start": v(499.1, 322.6) * mm, "mid": v(495.56, 321.14) * mm, "end": v(494.1, 317.6) * mm});
            skPoint(sketch, "E66.visualSharp", {"position": v(494.1, 312.6) * mm});
            skArc(sketch, "E66.filletArc", {"start": v(494.1, 317.6) * mm, "mid": v(495.56, 314.07) * mm, "end": v(499.1, 312.6) * mm});
            skPoint(sketch, "E67.visualSharp", {"position": v(509.1, 312.6) * mm});
            skArc(sketch, "E67.filletArc", {"start": v(504.1, 312.6) * mm, "mid": v(507.63, 314.07) * mm, "end": v(509.1, 317.6) * mm});
            skLineSegment(sketch, "E68", {"start": v(509.1, 479.6) * mm, "end": v(494.1, 479.6) * mm, "construction": true});
            skLineSegment(sketch, "E69", {"start": v(501.6, 484.6) * mm, "end": v(501.6, 474.6) * mm, "construction": true});
            skLineSegment(sketch, "E70", {"start": v(494.1, 317.6) * mm, "end": v(509.1, 317.6) * mm, "construction": true});
            skLineSegment(sketch, "E71", {"start": v(501.6, 322.6) * mm, "end": v(501.6, 312.6) * mm, "construction": true});
            skCircle(sketch, "E72", {"center": v(576.6, 479.6) * mm, "radius": 5 * mm});
            skCircle(sketch, "E73", {"center": v(576.6, 317.6) * mm, "radius": 5 * mm});
            skLineSegment(sketch, "E74.bottom", {"start": v(501.6, 479.6) * mm, "end": v(576.6, 479.6) * mm, "construction": true});
            skLineSegment(sketch, "E74.right", {"start": v(576.6, 479.6) * mm, "end": v(576.6, 317.6) * mm, "construction": true});
            skPoint(sketch, "E75", {"position": v(501.6, 317.6) * mm});
            skLineSegment(sketch, "E76.bottom", {"start": v(456.6, 499.6) * mm, "end": v(616.6, 499.6) * mm});
            skLineSegment(sketch, "E76.top", {"start": v(456.6, 297.6) * mm, "end": v(616.6, 297.6) * mm});
            skLineSegment(sketch, "E76.left", {"start": v(456.6, 499.6) * mm, "end": v(456.6, 297.6) * mm});
            skLineSegment(sketch, "E76.right", {"start": v(616.6, 499.6) * mm, "end": v(616.6, 297.6) * mm});
            skSolve(sketch);
        }
        {
            var Q0;
            Q0=makeQuery(id+"F5.imprint","IMPRINT",FACE,{"disambiguationData":[TD([[makeQuery(id+"F5.imprint","IMPRINT",EDGE,{"derivedFrom":sQuery(id+"F5.wireOp",EDGE,"E58.bottom")}),1.0]])]});
            extrude(context, id + "F6", {"entities" : qUnion([Q0]), "depth" : 6 * mm});
        }
    });
